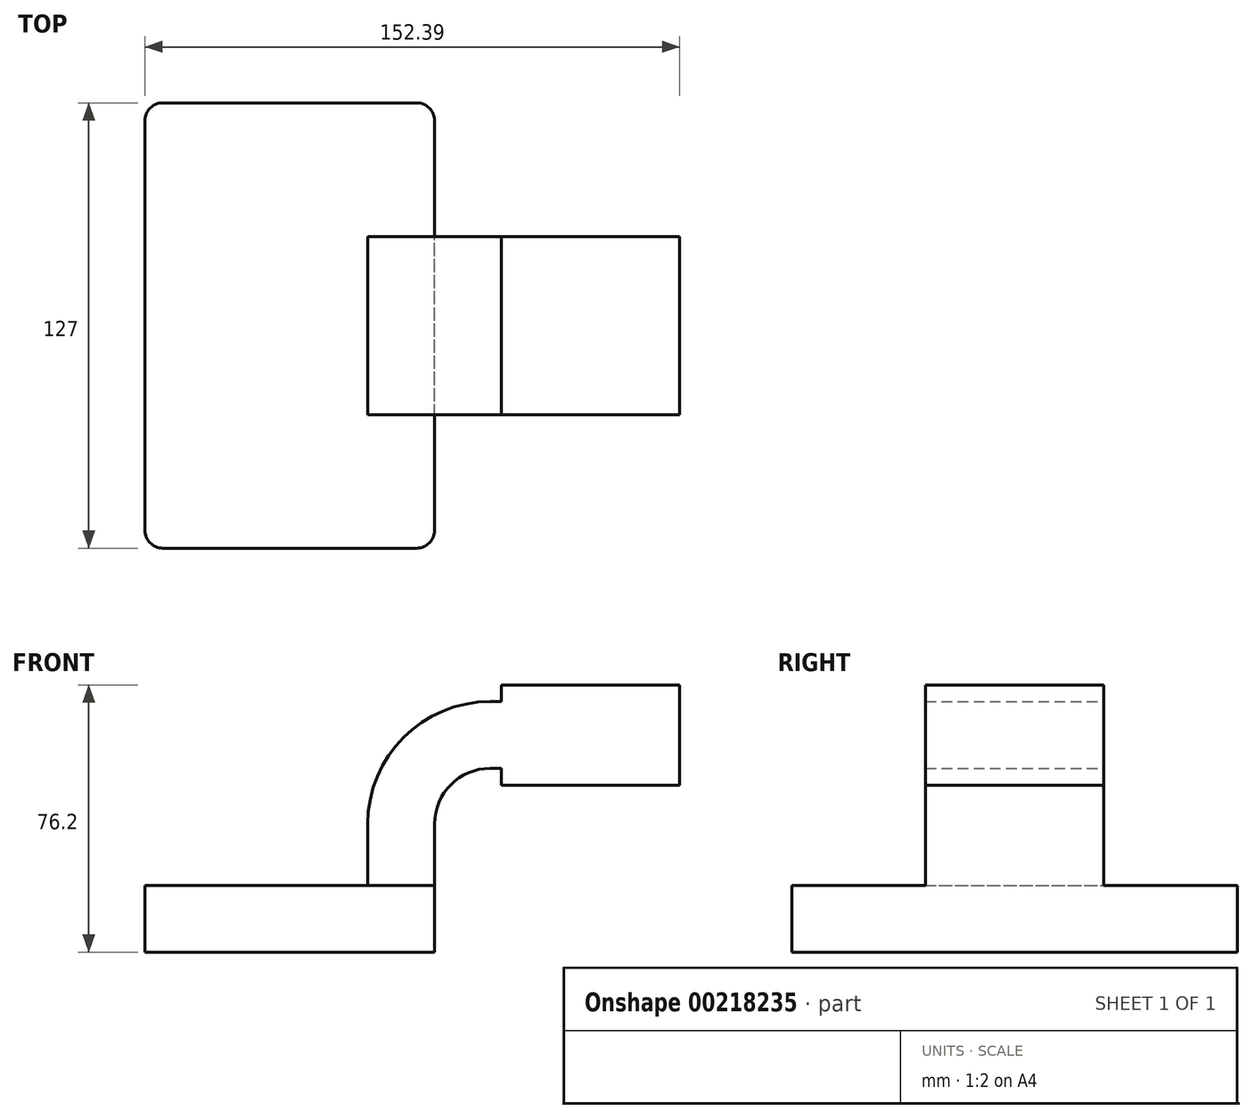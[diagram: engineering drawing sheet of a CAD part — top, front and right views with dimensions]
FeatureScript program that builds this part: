
annotation { "Feature Type Name" : "Feature", "Feature Type Description" : "" }
export const myFeature = defineFeature(function(context is Context, id is Id, definition is map)
    precondition{}
    {
        {
            var Q0;
            Q0=qCreatedBy(makeId("Front.planeOp"),FACE);
            var sketch = newSketch(context, id + "F0", { "sketchPlane" : qUnion([Q0])});
            skLineSegment(sketch, "E0.bottom", {"start": v(-41.28, 9.52) * mm, "end": v(41.28, 9.53) * mm});
            skLineSegment(sketch, "E0.top", {"start": v(-41.28, -9.53) * mm, "end": v(41.28, -9.53) * mm});
            skLineSegment(sketch, "E0.left", {"start": v(-41.28, 9.52) * mm, "end": v(-41.28, -9.53) * mm});
            skLineSegment(sketch, "E0.right", {"start": v(41.28, 9.53) * mm, "end": v(41.28, -9.52) * mm});
            skPoint(sketch, "E0.middle", {"position": v(0, 0) * mm});
            skLineSegment(sketch, "E1", {"start": v(41.27, 9.53) * mm, "end": v(41.27, 27) * mm});
            skArc(sketch, "E2", {"start": v(41.27, 27) * mm, "mid": v(45.92, 38.23) * mm, "end": v(57.15, 42.88) * mm});
            skLineSegment(sketch, "E3.bottom", {"start": v(60.32, 66.67) * mm, "end": v(111.12, 66.67) * mm});
            skLineSegment(sketch, "E3.top", {"start": v(60.32, 38.1) * mm, "end": v(111.12, 38.1) * mm});
            skLineSegment(sketch, "E3.left", {"start": v(60.32, 66.68) * mm, "end": v(60.32, 38.1) * mm});
            skLineSegment(sketch, "E3.right", {"start": v(111.12, 66.68) * mm, "end": v(111.12, 38.1) * mm});
            skPoint(sketch, "E3.middle", {"position": v(85.72, 52.39) * mm});
            skLineSegment(sketch, "E4", {"start": v(57.15, 42.88) * mm, "end": v(94.01, 42.88) * mm});
            skLineSegment(sketch, "E5.0", {"start": v(57.15, 27.64) * mm, "end": v(94.01, 27.64) * mm});
            skArc(sketch, "E5.1", {"start": v(56.52, 27) * mm, "mid": v(56.7, 27.45) * mm, "end": v(57.15, 27.64) * mm});
            skLineSegment(sketch, "E5.2", {"start": v(56.52, 9.53) * mm, "end": v(56.52, 27) * mm});
            skLineSegment(sketch, "E6.0", {"start": v(57.15, 61.93) * mm, "end": v(94.01, 61.93) * mm});
            skArc(sketch, "E6.1", {"start": v(22.22, 27) * mm, "mid": v(32.45, 51.7) * mm, "end": v(57.15, 61.93) * mm});
            skLineSegment(sketch, "E6.2", {"start": v(22.22, 9.53) * mm, "end": v(22.22, 27) * mm});
            skFitSpline(sketch, "E7", {"points": [v(-41.28, 9.52) * mm, v(57.15, 61.93) * mm], "startDerivative": vector(-2.27, 148.83) * mm, "endDerivative": vector(135.24, -0.08) * mm});
            skSolve(sketch);
        }
        {
            var Q0;
            Q0=makeQuery(id+"F0.imprint","IMPRINT",FACE,{"disambiguationData":[TD([[makeQuery(id+"F0.imprint","IMPRINT",EDGE,{"derivedFrom":sQuery(id+"F0.wireOp",EDGE,"E0.top")}),1.0]])]});
            extrude(context, id + "F1", {"entities" : qUnion([Q0]), "endBound" : BoundingType.SYMMETRIC, "depth" : 127 * mm});
        }
        {
            var Q0;
            {var subQ6=sQuery(id+"F0.wireOp",EDGE,"E1");Q0=makeQuery(id+"F0.imprint","IMPRINT",FACE,{"disambiguationData":[TD([[makeQuery(id+"F0.imprint","IMPRINT",EDGE,{"derivedFrom":subQ6}),1.0]])]});}
            var Q1;
            {var subQ3=sQuery(id+"F0.wireOp",EDGE,"E3.bottom");Q1=makeQuery(id+"F0.imprint","IMPRINT",FACE,{"disambiguationData":[TD([[makeQuery(id+"F0.imprint","IMPRINT",EDGE,{"derivedFrom":subQ3}),-1.0]])]});}
            extrude(context, id + "F2", {"entities" : qUnion([Q0, Q1]), "operationType" : NewBodyOperationType.ADD, "endBound" : BoundingType.SYMMETRIC, "depth" : 50.8 * mm});
        }
        {
            var Q0;
            Q0=makeQuery(id+"F0.imprint","IMPRINT",FACE,{"disambiguationData":[TD([[makeQuery(id+"F0.imprint","IMPRINT",EDGE,{"derivedFrom":sQuery(id+"F0.wireOp",EDGE,"E6.1")}),1.0]])]});
            extrude(context, id + "F3", {"entities" : qUnion([Q0]), "operationType" : NewBodyOperationType.ADD, "endBound" : BoundingType.SYMMETRIC, "depth" : 15.88 * mm});
        }
        {
            var Q0;
            Q0=makeQuery(id+"F1.opExtrude","CAP_EDGE",EDGE,{"disambiguationData":[OSD([sQuery(id+"F0.wireOp",EDGE,"E0.left")])],"isStart":false});
            var Q1;
            Q1=makeQuery(id+"F1.opExtrude","CAP_EDGE",EDGE,{"disambiguationData":[OSD([sQuery(id+"F0.wireOp",EDGE,"E0.right")])],"isStart":false});
            var Q2;
            Q2=makeQuery(id+"F1.opExtrude","CAP_EDGE",EDGE,{"disambiguationData":[OSD([sQuery(id+"F0.wireOp",EDGE,"E0.right")])],"isStart":true});
            var Q3;
            Q3=makeQuery(id+"F1.opExtrude","CAP_EDGE",EDGE,{"disambiguationData":[OSD([sQuery(id+"F0.wireOp",EDGE,"E0.left")])],"isStart":true});
            fillet(context, id + "F4", {"entities" : qUnion([Q0, Q1, Q2, Q3]), "radius" : 5.08 * mm, "tangentPropagation" : true, "allowEdgeOverflow" : false});
        }
    });
